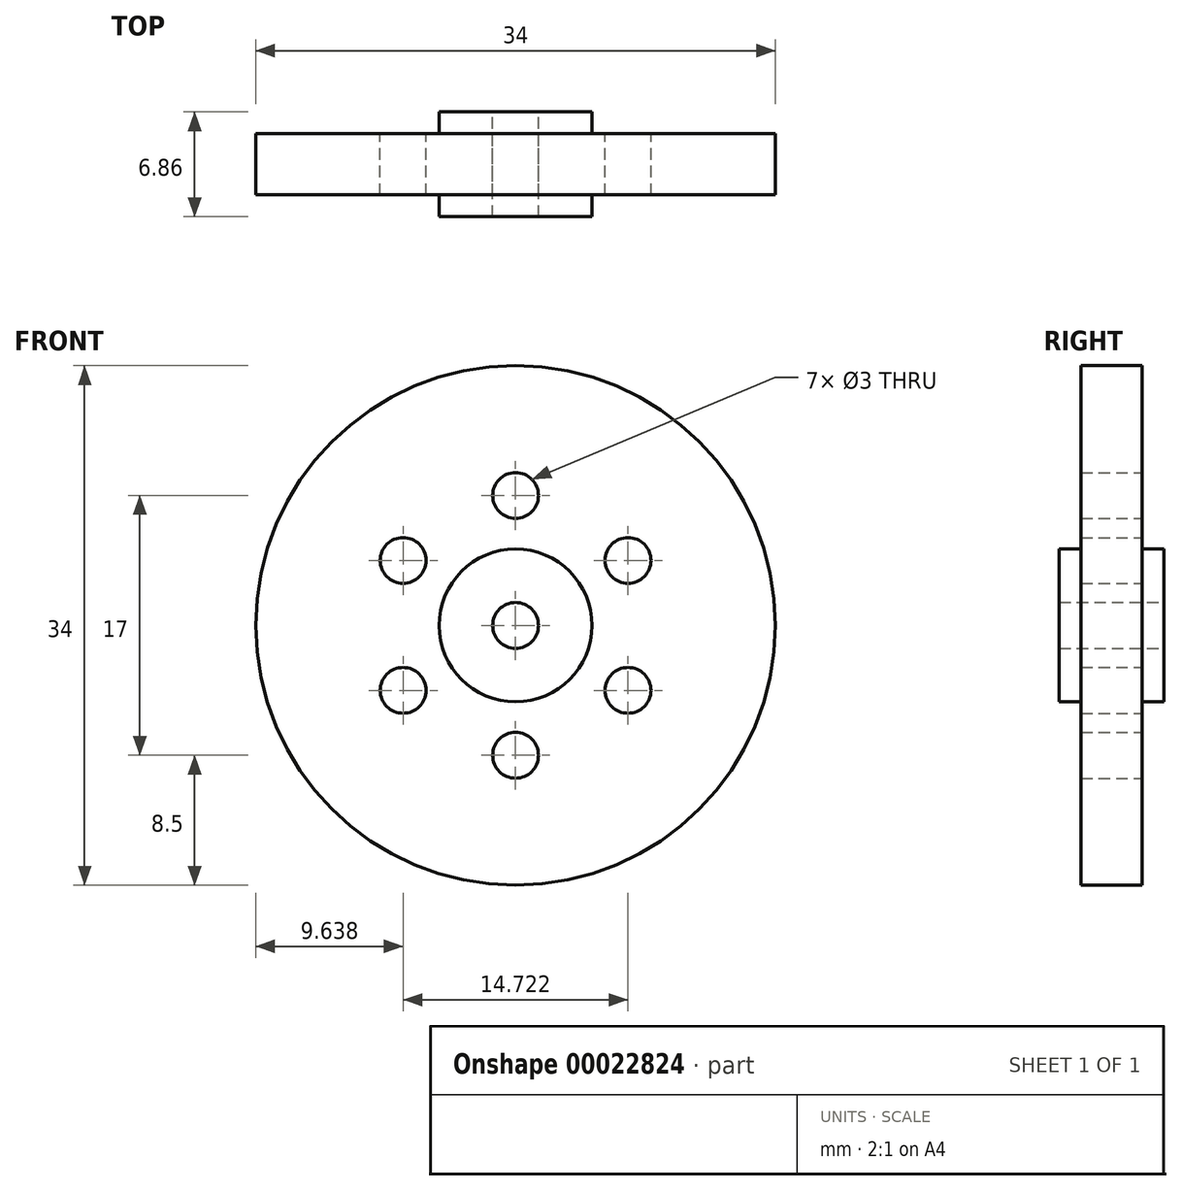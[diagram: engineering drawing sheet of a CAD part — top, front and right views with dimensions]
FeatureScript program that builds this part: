
annotation { "Feature Type Name" : "Feature", "Feature Type Description" : "" }
export const myFeature = defineFeature(function(context is Context, id is Id, definition is map)
    precondition{}
    {
        {
            var Q0;
            Q0=qCreatedBy(makeId("Front.planeOp"),FACE);
            var sketch = newSketch(context, id + "F0", { "sketchPlane" : qUnion([Q0])});
            skCircle(sketch, "E0", {"center": v(-31.44, 0) * mm, "radius": 17 * mm});
            skCircle(sketch, "E1", {"center": v(-31.44, 0) * mm, "radius": 5 * mm});
            skCircle(sketch, "E2", {"center": v(-31.44, 0) * mm, "radius": 1.5 * mm});
            skLineSegment(sketch, "E3", {"start": v(-31.44, 5) * mm, "end": v(-31.44, 7) * mm});
            skCircle(sketch, "E4", {"center": v(-31.44, 8.5) * mm, "radius": 1.5 * mm});
            skCircle(sketch, "E5.1.0", {"center": v(-38.8, 4.25) * mm, "radius": 1.5 * mm});
            skCircle(sketch, "E5.2.0", {"center": v(-38.8, -4.25) * mm, "radius": 1.5 * mm});
            skCircle(sketch, "E5.3.0", {"center": v(-31.44, -8.5) * mm, "radius": 1.5 * mm});
            skCircle(sketch, "E6.1.4.0", {"center": v(-24.08, -4.25) * mm, "radius": 1.5 * mm});
            skCircle(sketch, "E6.1.5.0", {"center": v(-24.08, 4.25) * mm, "radius": 1.5 * mm});
            skSolve(sketch);
        }
        {
            var Q0;
            Q0=makeQuery(id+"F0.imprint","IMPRINT",FACE,{"disambiguationData":[TD([[makeQuery(id+"F0.imprint","IMPRINT",EDGE,{"derivedFrom":sQuery(id+"F0.wireOp",EDGE,"E0")}),1.0]])]});
            extrude(context, id + "F1", {"entities" : qUnion([Q0]), "endBound" : BoundingType.SYMMETRIC, "depth" : 4 * mm});
        }
        {
            var Q0;
            Q0=makeQuery(id+"F0.imprint","IMPRINT",FACE,{"disambiguationData":[TD([[makeQuery(id+"F0.imprint","IMPRINT",EDGE,{"derivedFrom":sQuery(id+"F0.wireOp",EDGE,"E1")}),1.0]])]});
            var Q1;
            Q1=sQuery(id+"F0.wireOp",EDGE,"E1");
            extrude(context, id + "F2", {"entities" : qUnion([Q0]), "operationType" : NewBodyOperationType.ADD, "surfaceEntities" : qUnion([Q1]), "endBound" : BoundingType.SYMMETRIC, "depth" : 6.86 * mm});
        }
    });
